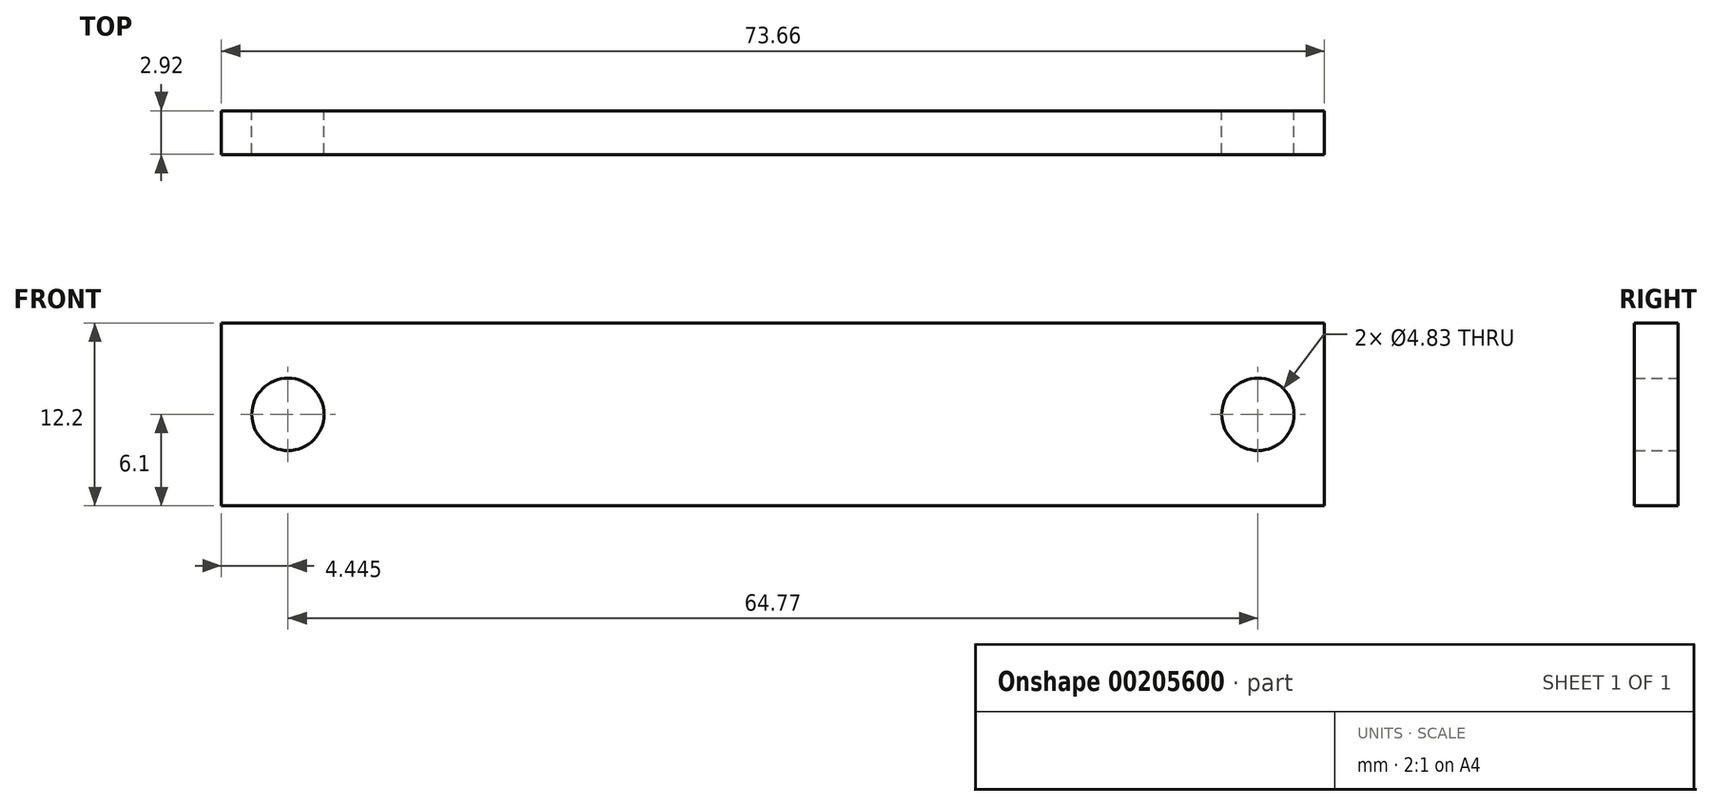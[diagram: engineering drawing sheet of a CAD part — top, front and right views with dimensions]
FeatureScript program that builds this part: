
annotation { "Feature Type Name" : "Feature", "Feature Type Description" : "" }
export const myFeature = defineFeature(function(context is Context, id is Id, definition is map)
    precondition{}
    {
        {
            var Q0;
            Q0=qCreatedBy(makeId("Front.planeOp"),FACE);
            var sketch = newSketch(context, id + "F0", { "sketchPlane" : qUnion([Q0])});
            skLineSegment(sketch, "E0.bottom", {"start": v(-36.83, 6.1) * mm, "end": v(36.83, 6.1) * mm});
            skLineSegment(sketch, "E0.top", {"start": v(-36.83, -6.1) * mm, "end": v(36.83, -6.1) * mm});
            skLineSegment(sketch, "E0.left", {"start": v(-36.83, 6.1) * mm, "end": v(-36.83, -6.1) * mm});
            skLineSegment(sketch, "E0.right", {"start": v(36.83, 6.1) * mm, "end": v(36.83, -6.1) * mm});
            skPoint(sketch, "E0.middle", {"position": v(0, 0) * mm});
            skCircle(sketch, "E1", {"center": v(-32.39, 0) * mm, "radius": 2.41 * mm});
            skCircle(sketch, "E2", {"center": v(32.39, 0) * mm, "radius": 2.41 * mm});
            skSolve(sketch);
        }
        {
            var Q0;
            Q0=qSketchRegion(id+"F0",true);
            extrude(context, id + "F1", {"entities" : qUnion([Q0]), "flatOperationType" : FlatOperationType.REMOVE, "offsetDistance" : 25.4 * mm, "depth" : 2.92 * mm, "domain" : OperationDomain.MODEL});
        }
    });
